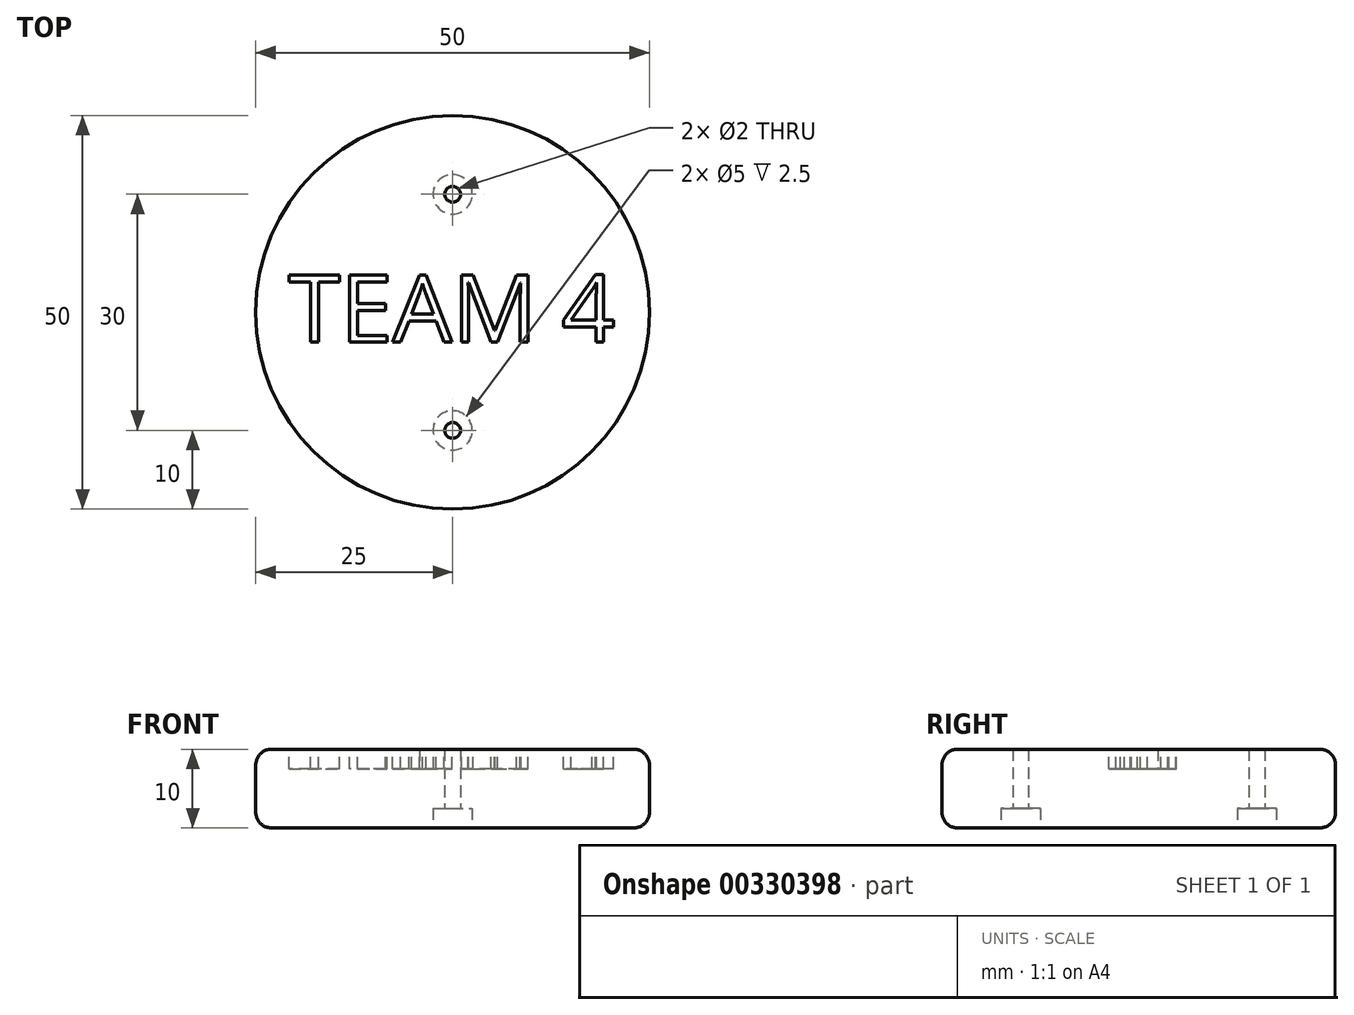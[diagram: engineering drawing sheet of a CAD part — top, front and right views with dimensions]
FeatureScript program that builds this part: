
annotation { "Feature Type Name" : "Feature", "Feature Type Description" : "" }
export const myFeature = defineFeature(function(context is Context, id is Id, definition is map)
    precondition{}
    {
        {
            var Q0;
            Q0=qCreatedBy(makeId("Top.planeOp"),FACE);
            var sketch = newSketch(context, id + "F0", { "sketchPlane" : qUnion([Q0])});
            skCircle(sketch, "E0", {"center": v(0, 0) * mm, "radius": 25 * mm});
            skSolve(sketch);
        }
        {
            var Q0;
            Q0=qSketchRegion(id+"F0",true);
            extrude(context, id + "F1", {"entities" : qUnion([Q0]), "depth" : 10 * mm});
        }
        {
            var Q0;
            Q0=makeQuery(id+"F1.opExtrude","CAP_EDGE",EDGE,{"disambiguationData":[OSD([sQuery(id+"F0.wireOp",EDGE,"E0")])],"isStart":false});
            var Q1;
            Q1=makeQuery(id+"F1.opExtrude","CAP_EDGE",EDGE,{"disambiguationData":[OSD([sQuery(id+"F0.wireOp",EDGE,"E0")])],"isStart":true});
            fillet(context, id + "F2", {"entities" : qUnion([Q0, Q1]), "radius" : 2 * mm, "tangentPropagation" : true, "allowEdgeOverflow" : false});
        }
        {
            var Q0;
            Q0=makeQuery(id+"F1.opExtrude","CAP_FACE",FACE,{"disambiguationData":[OSD([sQuery(id+"F0.wireOp",EDGE,"E0")])],"isStart":true});
            var sketch = newSketch(context, id + "F3", { "sketchPlane" : qUnion([Q0])});
            skPoint(sketch, "E1", {"position": v(0, 15) * mm});
            skPoint(sketch, "E2", {"position": v(0, -15) * mm});
            skSolve(sketch);
        }
        {
            var Q0;
            Q0=sQuery(id+"F3.wireOp",VERTEX,"E1");
            var Q1;
            Q1=sQuery(id+"F3.wireOp",VERTEX,"E2");
            var Q2;
            Q2=makeQuery(id+"F1.opExtrude","SWEPT_BODY",BODY,{"disambiguationData":[OSD([sQuery(id+"F0.wireOp",EDGE,"E0")])]});
            hole(context, id + "F4", {"style" : HoleStyle.C_BORE, "endStyle" : HoleEndStyle.THROUGH, "holeDiameter" : 2 * mm, "cBoreDiameter" : 5 * mm, "cBoreDepth" : 2.5 * mm, "startFromSketch" : true, "locations" : qUnion([Q0, Q1]), "scope" : qUnion([Q2]), "isTappedThrough" : true});
        }
        {
            var Q0;
            Q0=makeQuery(id+"F1.opExtrude","CAP_FACE",FACE,{"disambiguationData":[OSD([sQuery(id+"F0.wireOp",EDGE,"E0")])],"isStart":false});
            var sketch = newSketch(context, id + "F5", { "sketchPlane" : qUnion([Q0])});
            skText(sketch, "E3", { "text": "TEAM 4\n", "fontName": "OpenSans-Regular.ttf"});
            const initialGuessF5  = {"E3": [-0.02085, -0.0038, 1, 0, 0.0086]};
            skSetInitialGuess(sketch, initialGuessF5);
            skSolve(sketch);
        }
        {
            var Q0;
            Q0 = qSketchRegion(id + "F5", true);
            extrude(context, id + "F6", {"entities" : qUnion([Q0]), "operationType" : NewBodyOperationType.REMOVE, "oppositeDirection" : true, "depth" : 2.5 * mm});
        }
    });
